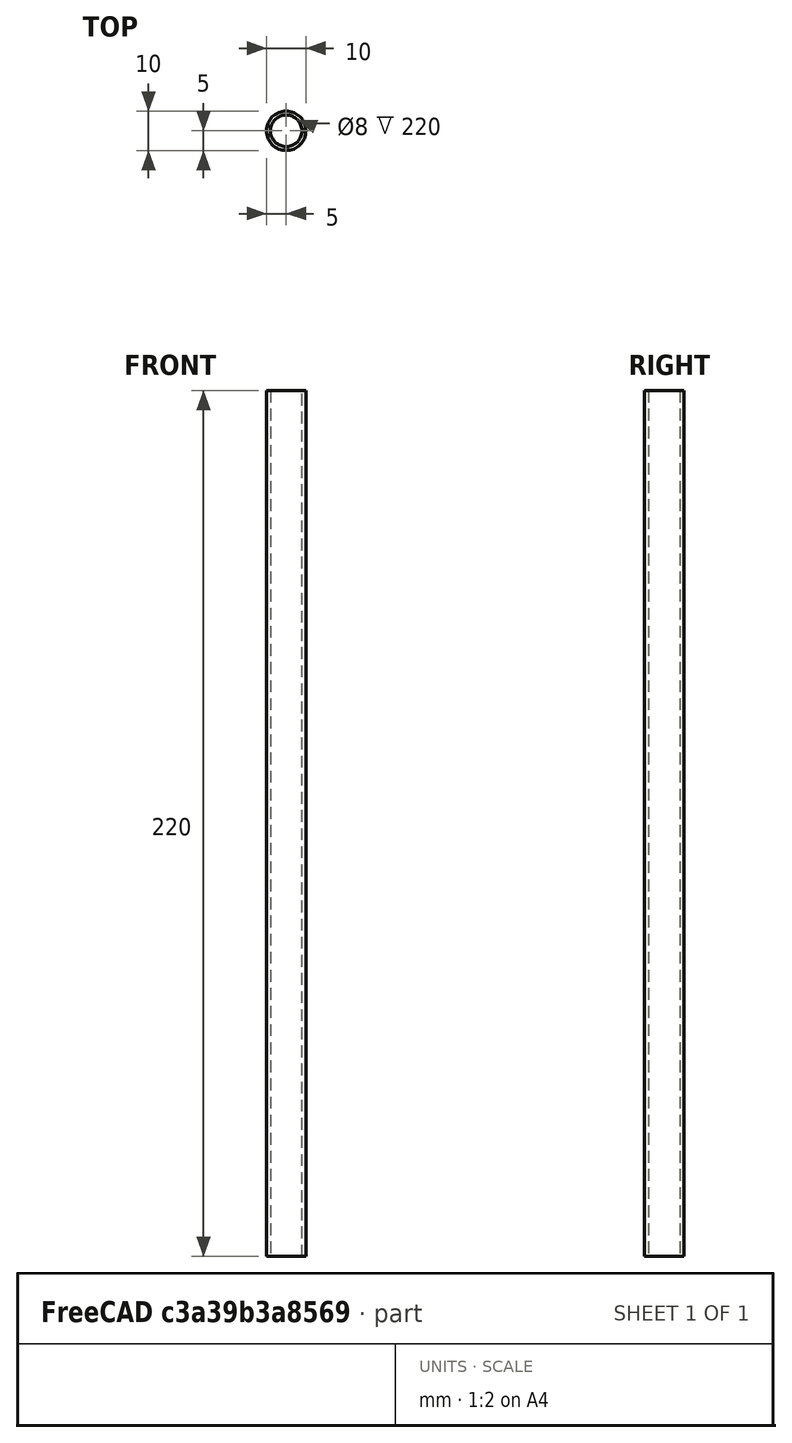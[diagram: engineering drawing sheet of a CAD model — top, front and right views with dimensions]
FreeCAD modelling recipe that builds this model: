
FCSTD DOCUMENT  (FreeCAD 0.19R24276 (Git))
Label: Tube_220_for_arm_250
License: All rights reserved
LicenseURL: http://en.wikipedia.org/wiki/All_rights_reserved
objects: Sketcher::SketchObject×1, PartDesign::Pad×1, PartDesign::Body×1
note: 4 computed .brp shape members not serialized (recipe doc carries the construction recipe); baked Part::Feature solids carry a one-line shape summary decoded from their .brp

FEATURE [Sketcher::SketchObject] Sketch
  FullyConstrained = true
  MapMode = 5
  Support = -> [XY_Plane]
  sketch-geometry (2):
    g0: Circle CenterX=0 CenterY=0 CenterZ=0 NormalX=0 NormalY=0 NormalZ=1 AngleXU=0 Radius=4
    g1: Circle CenterX=0 CenterY=0 CenterZ=0 NormalX=0 NormalY=0 NormalZ=1 AngleXU=0 Radius=5
  constraints (4):
    c: Coincident(g0,g-1)
    c: Coincident(g1,g0)
    c: Diameter(g0) = 8
    c: Diameter(g1) = 10
FEATURE [PartDesign::Pad] Pad
  Direction = (1,1,1)
  Length = 220
  Length2 = 100
  Profile = -> Sketch
  Type = 0
FEATURE [PartDesign::Body] Body
  Group = -> [Sketch,Pad]
  Origin = -> Origin
  Tip = -> Pad
